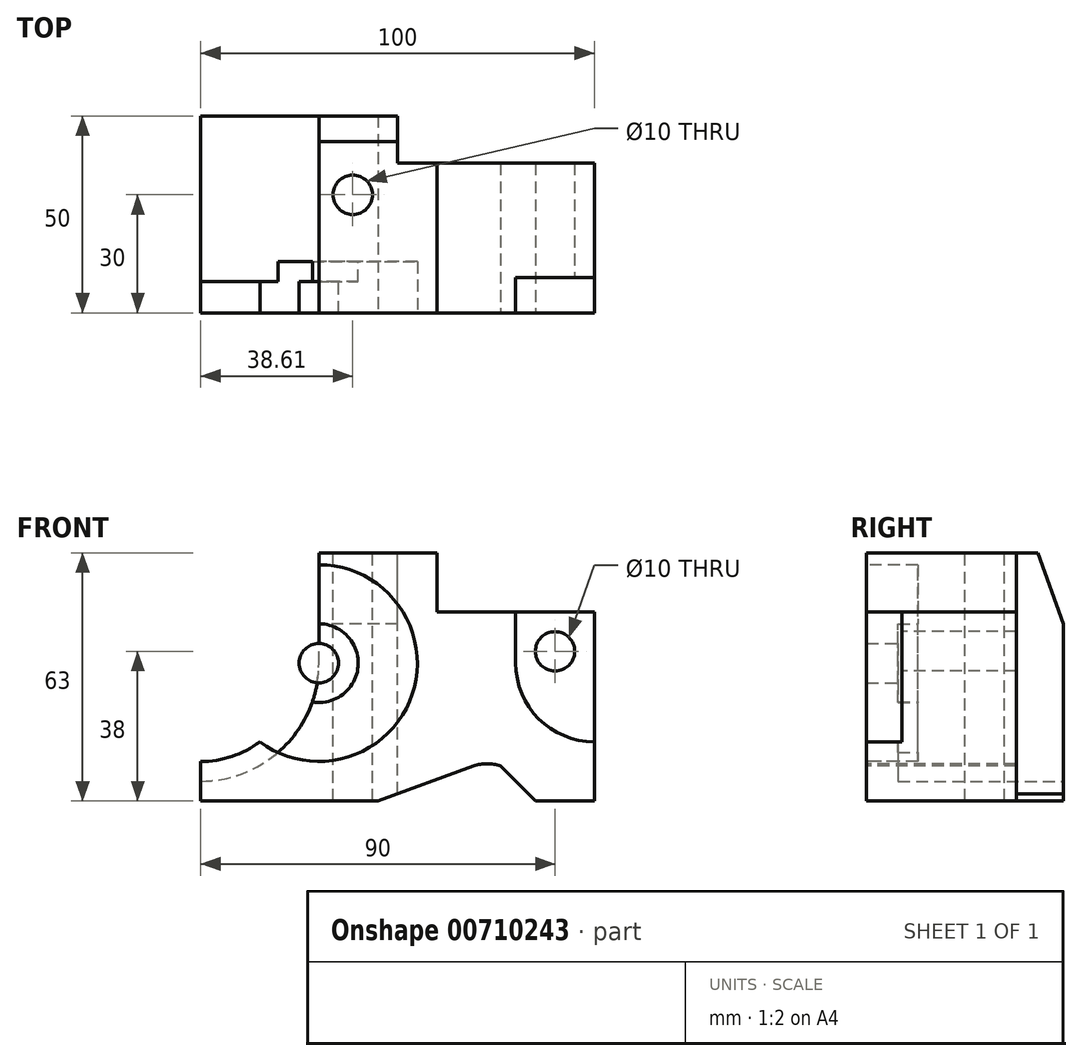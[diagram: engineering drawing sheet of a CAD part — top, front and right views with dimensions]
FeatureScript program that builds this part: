
annotation { "Feature Type Name" : "Feature", "Feature Type Description" : "" }
export const myFeature = defineFeature(function(context is Context, id is Id, definition is map)
    precondition{}
    {
        {
            var Q0;
            Q0=qCreatedBy(makeId("Top.planeOp"),FACE);
            var sketch = newSketch(context, id + "F0", { "sketchPlane" : qUnion([Q0])});
            skLineSegment(sketch, "E0.bottom", {"start": v(-50, 25) * mm, "end": v(50, 25) * mm});
            skLineSegment(sketch, "E0.top", {"start": v(-50, -25) * mm, "end": v(50, -25) * mm});
            skLineSegment(sketch, "E0.left", {"start": v(-50, 25) * mm, "end": v(-50, -25) * mm});
            skLineSegment(sketch, "E0.right", {"start": v(50, 25) * mm, "end": v(50, -25) * mm});
            skPoint(sketch, "E0.middle", {"position": v(0, 0) * mm});
            skSolve(sketch);
        }
        {
            var Q0;
            Q0=makeQuery(id+"F0.imprint","IMPRINT",FACE,{"disambiguationData":[TD([[makeQuery(id+"F0.imprint","IMPRINT",EDGE,{"derivedFrom":sQuery(id+"F0.wireOp",EDGE,"E0.bottom")}),-1.0]])]});
            extrude(context, id + "F1", {"entities" : qUnion([Q0]), "depth" : 63 * mm, "offsetDistance" : 25 * mm});
        }
        {
            var Q0;
            Q0=makeQuery(id+"F1.opExtrude","CAP_FACE",FACE,{"disambiguationData":[OSD([sQuery(id+"F0.wireOp",EDGE,"E0.bottom"),sQuery(id+"F0.wireOp",EDGE,"E0.top"),sQuery(id+"F0.wireOp",EDGE,"E0.left"),sQuery(id+"F0.wireOp",EDGE,"E0.right")])],"isStart":false});
            var sketch = newSketch(context, id + "F2", { "sketchPlane" : qUnion([Q0])});
            skLineSegment(sketch, "E1.bottom", {"start": v(50, 25) * mm, "end": v(0, 25) * mm});
            skLineSegment(sketch, "E1.top", {"start": v(50, 13) * mm, "end": v(0, 13) * mm});
            skLineSegment(sketch, "E1.left", {"start": v(50, 25) * mm, "end": v(50, 13) * mm});
            skLineSegment(sketch, "E1.right", {"start": v(0, 25) * mm, "end": v(0, 13) * mm});
            skSolve(sketch);
        }
        {
            var Q0;
            Q0=makeQuery(id+"F2.imprint","IMPRINT",FACE,{"disambiguationData":[TD([[makeQuery(id+"F2.imprint","IMPRINT",EDGE,{"derivedFrom":sQuery(id+"F2.wireOp",EDGE,"E1.bottom")}),-1.0]])]});
            extrude(context, id + "F3", {"entities" : qUnion([Q0]), "operationType" : NewBodyOperationType.REMOVE, "endBound" : BoundingType.THROUGH_ALL, "oppositeDirection" : true, "depth" : 25 * mm, "offsetDistance" : 25 * mm});
        }
        {
            var Q0;
            Q0=makeQuery(id+"F1.opExtrude","SWEPT_FACE",FACE,{"disambiguationData":[OSD([sQuery(id+"F0.wireOp",EDGE,"E0.top")])]});
            var sketch = newSketch(context, id + "F4", { "sketchPlane" : qUnion([Q0])});
            skLineSegment(sketch, "E2", {"start": v(-5, 0) * mm, "end": v(19.31, 8.85) * mm});
            skArc(sketch, "E3", {"start": v(26.15, 8.85) * mm, "mid": v(22.73, 9.45) * mm, "end": v(19.31, 8.85) * mm});
            skLineSegment(sketch, "E4", {"start": v(26.15, 8.85) * mm, "end": v(35, 0) * mm});
            skSolve(sketch);
        }
        {
            var Q0;
            {var subQ0=sQuery(id+"F4.wireOp",EDGE,"E2");Q0=makeQuery(id+"F4.imprint","IMPRINT",FACE,{"disambiguationData":[TD([[makeQuery(id+"F4.imprint","IMPRINT",EDGE,{"derivedFrom":subQ0}),-1.0]])]});}
            extrude(context, id + "F5", {"entities" : qUnion([Q0]), "operationType" : NewBodyOperationType.REMOVE, "endBound" : BoundingType.THROUGH_ALL, "oppositeDirection" : true, "depth" : 25 * mm, "offsetDistance" : 25 * mm});
        }
        {
            var Q0;
            Q0=makeQuery(id+"F1.opExtrude","SWEPT_FACE",FACE,{"disambiguationData":[OSD([sQuery(id+"F0.wireOp",EDGE,"E0.top")])]});
            var sketch = newSketch(context, id + "F6", { "sketchPlane" : qUnion([Q0])});
            skCircle(sketch, "E5", {"center": v(-20, 35) * mm, "radius": 25 * mm});
            skSolve(sketch);
        }
        {
            var Q0;
            Q0=makeQuery(id+"F6.imprint","IMPRINT",FACE,{"disambiguationData":[TD([[makeQuery(id+"F6.imprint","IMPRINT",EDGE,{"derivedFrom":sQuery(id+"F6.wireOp",EDGE,"E5")}),1.0]])]});
            extrude(context, id + "F7", {"entities" : qUnion([Q0]), "operationType" : NewBodyOperationType.REMOVE, "oppositeDirection" : true, "depth" : 13 * mm, "offsetDistance" : 25 * mm});
        }
        {
            var Q0;
            Q0=makeQuery(id+"F7.boolean.opBoolean","COPY",FACE,{"derivedFrom":makeQuery(id+"F7.opExtrude","CAP_FACE",FACE,{"disambiguationData":[OSD([sQuery(id+"F6.wireOp",EDGE,"E5")])],"isStart":false})});
            var sketch = newSketch(context, id + "F8", { "sketchPlane" : qUnion([Q0])});
            skCircle(sketch, "E6", {"center": v(-20, 35) * mm, "radius": 5 * mm});
            skCircle(sketch, "E7", {"center": v(-20, 35) * mm, "radius": 10 * mm});
            skSolve(sketch);
        }
        {
            var Q0;
            Q0=makeQuery(id+"F8.imprint","IMPRINT",FACE,{"disambiguationData":[TD([[makeQuery(id+"F8.imprint","IMPRINT",EDGE,{"derivedFrom":sQuery(id+"F8.wireOp",EDGE,"E6")}),-1.0]])]});
            extrude(context, id + "F9", {"entities" : qUnion([Q0]), "operationType" : NewBodyOperationType.ADD, "depth" : 5 * mm, "offsetDistance" : 25 * mm});
        }
        {
            var Q0;
            Q0=makeQuery(id+"F8.imprint","IMPRINT",FACE,{"disambiguationData":[TD([[makeQuery(id+"F8.imprint","IMPRINT",EDGE,{"derivedFrom":sQuery(id+"F8.wireOp",EDGE,"E6")}),1.0]])]});
            extrude(context, id + "F10", {"entities" : qUnion([Q0]), "operationType" : NewBodyOperationType.ADD, "depth" : 13 * mm, "offsetDistance" : 25 * mm});
        }
        {
            var Q0;
            Q0=makeQuery(id+"F1.opExtrude","SWEPT_FACE",FACE,{"disambiguationData":[OSD([sQuery(id+"F0.wireOp",EDGE,"E0.bottom")])]});
            var sketch = newSketch(context, id + "F11", { "sketchPlane" : qUnion([Q0])});
            skArc(sketch, "E8", {"start": v(20, 35) * mm, "mid": v(28.79, 13.79) * mm, "end": v(50, 5) * mm});
            skLineSegment(sketch, "E9", {"start": v(20, 35) * mm, "end": v(20, 63) * mm});
            skLineSegment(sketch, "E10", {"start": v(20, 63) * mm, "end": v(50, 63) * mm});
            skLineSegment(sketch, "E11", {"start": v(50, 63) * mm, "end": v(50, 5) * mm});
            skSolve(sketch);
        }
        {
            var Q0;
            Q0=makeQuery(id+"F11.imprint","IMPRINT",FACE,{"disambiguationData":[TD([[makeQuery(id+"F11.imprint","IMPRINT",EDGE,{"derivedFrom":sQuery(id+"F11.wireOp",EDGE,"E8")}),1.0]])]});
            extrude(context, id + "F12", {"entities" : qUnion([Q0]), "operationType" : NewBodyOperationType.REMOVE, "oppositeDirection" : true, "depth" : 42 * mm, "offsetDistance" : 25 * mm});
        }
        {
            var Q0;
            Q0=makeQuery(id+"F1.opExtrude","SWEPT_FACE",FACE,{"disambiguationData":[OSD([sQuery(id+"F0.wireOp",EDGE,"E0.top")])]});
            var sketch = newSketch(context, id + "F13", { "sketchPlane" : qUnion([Q0])});
            skArc(sketch, "E12", {"start": v(-50, 10) * mm, "mid": v(-42.1, 11.28) * mm, "end": v(-35, 15) * mm});
            skLineSegment(sketch, "E13", {"start": v(-50, 10) * mm, "end": v(-50, 63) * mm});
            skArc(sketch, "E14", {"start": v(-20, 60) * mm, "mid": v(-43.72, 42.9) * mm, "end": v(-35, 15) * mm});
            skLineSegment(sketch, "E15.0", {"start": v(-20, 60) * mm, "end": v(-20, 45) * mm});
            skLineSegment(sketch, "E16", {"start": v(-50, 63) * mm, "end": v(-20, 63) * mm});
            skLineSegment(sketch, "E17", {"start": v(-20, 63) * mm, "end": v(-20, 60) * mm});
            skSolve(sketch);
        }
        {
            var Q0;
            Q0=makeQuery(id+"F13.imprint","IMPRINT",FACE,{"disambiguationData":[TD([[makeQuery(id+"F13.imprint","IMPRINT",EDGE,{"derivedFrom":sQuery(id+"F13.wireOp",EDGE,"E12")}),1.0]])]});
            extrude(context, id + "F14", {"entities" : qUnion([Q0]), "operationType" : NewBodyOperationType.REMOVE, "oppositeDirection" : true, "depth" : 25 * mm, "offsetDistance" : 25 * mm});
        }
        {
            var Q0;
            Q0=makeQuery(id+"F14.boolean.opBoolean","MERGE",FACE,{"derivedFrom":[makeQuery(id+"F12.boolean.opBoolean","COPY",FACE,{"derivedFrom":makeQuery(id+"F12.opExtrude","SWEPT_FACE",FACE,{"disambiguationData":[OSD([sQuery(id+"F11.wireOp",EDGE,"E9")])]})}),makeQuery(id+"F14.opExtrude","SWEPT_FACE",FACE,{"disambiguationData":[OSD([sQuery(id+"F13.wireOp",EDGE,"E17")])]})]});
            var sketch = newSketch(context, id + "F15", { "sketchPlane" : qUnion([Q0])});
            skLineSegment(sketch, "E18", {"start": v(-25, 45) * mm, "end": v(-18.45, 63) * mm});
            skLineSegment(sketch, "E19", {"start": v(-18.45, 63) * mm, "end": v(-25, 63) * mm});
            skLineSegment(sketch, "E20", {"start": v(-25, 63) * mm, "end": v(-25, 45) * mm});
            skSolve(sketch);
        }
        {
            var Q0;
            Q0=makeQuery(id+"F15.imprint","IMPRINT",FACE,{"disambiguationData":[TD([[makeQuery(id+"F15.imprint","IMPRINT",EDGE,{"derivedFrom":sQuery(id+"F15.wireOp",EDGE,"E18")}),1.0]])]});
            extrude(context, id + "F16", {"entities" : qUnion([Q0]), "operationType" : NewBodyOperationType.REMOVE, "endBound" : BoundingType.THROUGH_ALL, "oppositeDirection" : true, "depth" : 25 * mm, "offsetDistance" : 25 * mm});
        }
        {
            var Q0;
            Q0=makeQuery(id+"F1.opExtrude","CAP_FACE",FACE,{"disambiguationData":[OSD([sQuery(id+"F0.wireOp",EDGE,"E0.bottom"),sQuery(id+"F0.wireOp",EDGE,"E0.top"),sQuery(id+"F0.wireOp",EDGE,"E0.left"),sQuery(id+"F0.wireOp",EDGE,"E0.right")])],"isStart":false});
            var sketch = newSketch(context, id + "F17", { "sketchPlane" : qUnion([Q0])});
            skCircle(sketch, "E21", {"center": v(-11.4, 5) * mm, "radius": 5 * mm});
            skSolve(sketch);
        }
        {
            var Q0;
            Q0=makeQuery(id+"F17.imprint","IMPRINT",FACE,{"disambiguationData":[TD([[makeQuery(id+"F17.imprint","IMPRINT",EDGE,{"derivedFrom":sQuery(id+"F17.wireOp",EDGE,"E21")}),1.0]])]});
            extrude(context, id + "F18", {"entities" : qUnion([Q0]), "operationType" : NewBodyOperationType.REMOVE, "endBound" : BoundingType.THROUGH_ALL, "oppositeDirection" : true, "depth" : 25 * mm, "offsetDistance" : 25 * mm});
        }
        {
            var Q0;
            Q0=makeQuery(id+"F1.opExtrude","CAP_FACE",FACE,{"disambiguationData":[OSD([sQuery(id+"F0.wireOp",EDGE,"E0.bottom"),sQuery(id+"F0.wireOp",EDGE,"E0.top"),sQuery(id+"F0.wireOp",EDGE,"E0.left"),sQuery(id+"F0.wireOp",EDGE,"E0.right")])],"isStart":false});
            var sketch = newSketch(context, id + "F19", { "sketchPlane" : qUnion([Q0])});
            skLineSegment(sketch, "E22.bottom", {"start": v(50, 13) * mm, "end": v(10, 13) * mm});
            skLineSegment(sketch, "E22.top", {"start": v(50, -25) * mm, "end": v(10, -25) * mm});
            skLineSegment(sketch, "E22.left", {"start": v(50, 13) * mm, "end": v(50, -25) * mm});
            skLineSegment(sketch, "E22.right", {"start": v(10, 13) * mm, "end": v(10, -25) * mm});
            skSolve(sketch);
        }
        {
            var Q0;
            Q0=makeQuery(id+"F19.imprint","IMPRINT",FACE,{"disambiguationData":[TD([[makeQuery(id+"F19.imprint","IMPRINT",EDGE,{"derivedFrom":sQuery(id+"F19.wireOp",EDGE,"E22.bottom")}),1.0]])]});
            extrude(context, id + "F20", {"entities" : qUnion([Q0]), "operationType" : NewBodyOperationType.REMOVE, "oppositeDirection" : true, "depth" : 15 * mm, "offsetDistance" : 25 * mm});
        }
        {
            var Q0;
            Q0=makeQuery(id+"F1.opExtrude","SWEPT_FACE",FACE,{"disambiguationData":[OSD([sQuery(id+"F0.wireOp",EDGE,"E0.top")])]});
            var sketch = newSketch(context, id + "F21", { "sketchPlane" : qUnion([Q0])});
            skArc(sketch, "E23", {"start": v(30, 35) * mm, "mid": v(35.86, 20.86) * mm, "end": v(50, 15) * mm});
            skLineSegment(sketch, "E24", {"start": v(30, 35) * mm, "end": v(30, 48) * mm});
            skLineSegment(sketch, "E25", {"start": v(30, 48) * mm, "end": v(50, 48) * mm});
            skLineSegment(sketch, "E26", {"start": v(50, 48) * mm, "end": v(50, 15) * mm});
            skSolve(sketch);
        }
        {
            var Q0;
            Q0=makeQuery(id+"F21.imprint","IMPRINT",FACE,{"disambiguationData":[TD([[makeQuery(id+"F21.imprint","IMPRINT",EDGE,{"derivedFrom":sQuery(id+"F21.wireOp",EDGE,"E23")}),1.0]])]});
            extrude(context, id + "F22", {"entities" : qUnion([Q0]), "operationType" : NewBodyOperationType.REMOVE, "oppositeDirection" : true, "depth" : 9 * mm, "offsetDistance" : 25 * mm});
        }
        {
            var Q0;
            Q0=makeQuery(id+"F22.boolean.opBoolean","COPY",FACE,{"derivedFrom":makeQuery(id+"F22.opExtrude","CAP_FACE",FACE,{"disambiguationData":[OSD([sQuery(id+"F21.wireOp",EDGE,"E23"),sQuery(id+"F21.wireOp",EDGE,"E24"),sQuery(id+"F21.wireOp",EDGE,"E25"),sQuery(id+"F21.wireOp",EDGE,"E26")])],"isStart":false})});
            var sketch = newSketch(context, id + "F23", { "sketchPlane" : qUnion([Q0])});
            skCircle(sketch, "E27", {"center": v(40, 38) * mm, "radius": 5 * mm});
            skSolve(sketch);
        }
        {
            var Q0;
            Q0=makeQuery(id+"F23.imprint","IMPRINT",FACE,{"disambiguationData":[TD([[makeQuery(id+"F23.imprint","IMPRINT",EDGE,{"derivedFrom":sQuery(id+"F23.wireOp",EDGE,"E27")}),1.0]])]});
            extrude(context, id + "F24", {"entities" : qUnion([Q0]), "operationType" : NewBodyOperationType.REMOVE, "endBound" : BoundingType.THROUGH_ALL, "oppositeDirection" : true, "depth" : 25 * mm, "offsetDistance" : 25 * mm});
        }
    });
